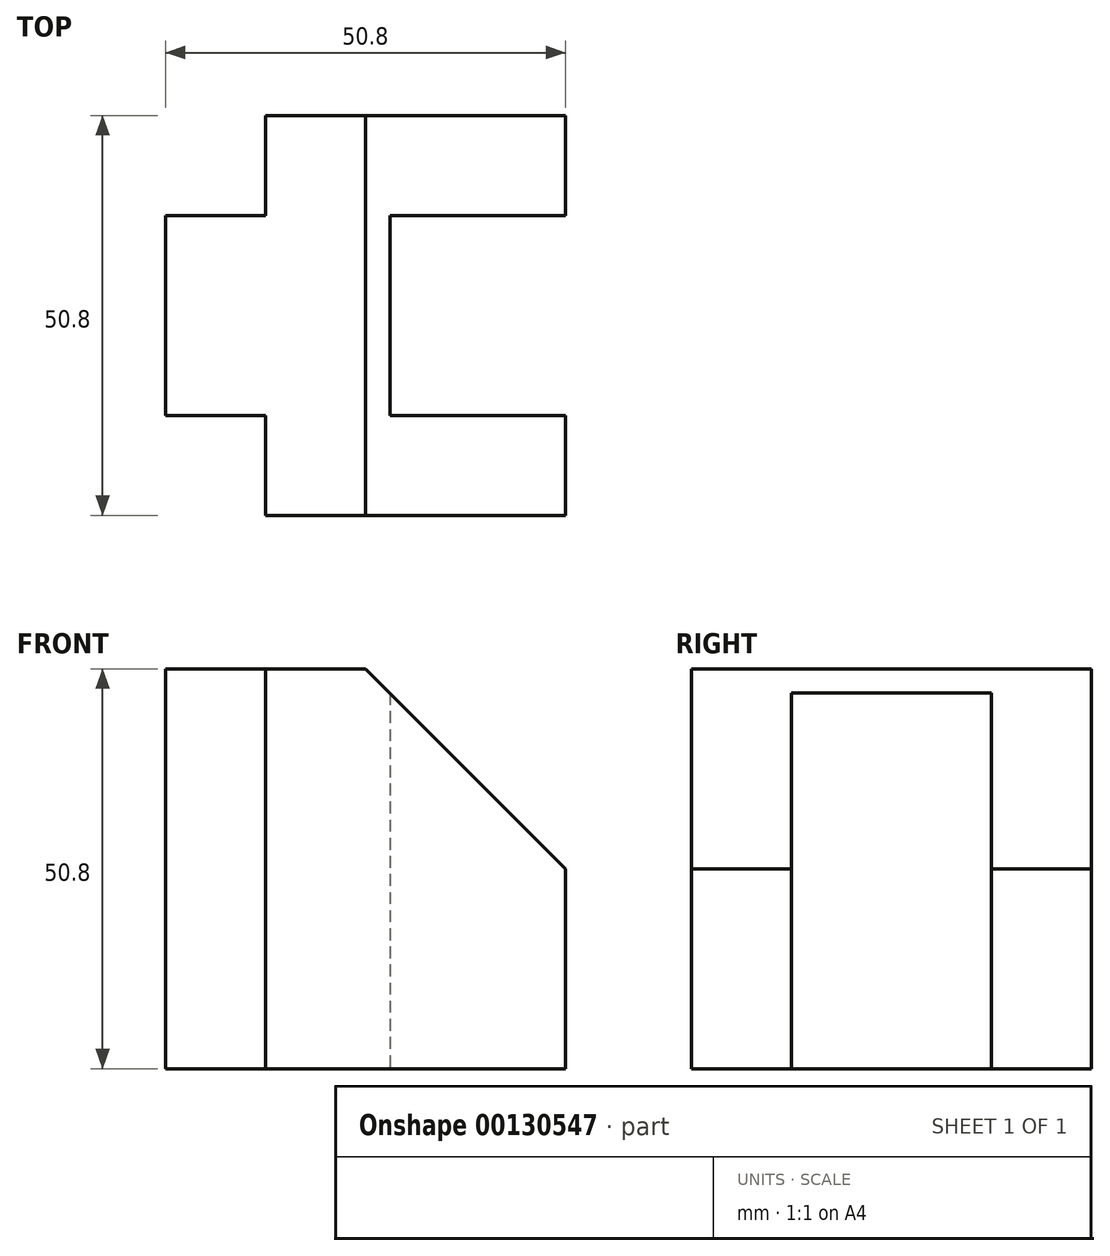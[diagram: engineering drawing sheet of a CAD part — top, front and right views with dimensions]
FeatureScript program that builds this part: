
annotation { "Feature Type Name" : "Feature", "Feature Type Description" : "" }
export const myFeature = defineFeature(function(context is Context, id is Id, definition is map)
    precondition{}
    {
        {
            var Q0;
            Q0=qCreatedBy(makeId("Front.planeOp"),FACE);
            var sketch = newSketch(context, id + "F0", { "sketchPlane" : qUnion([Q0])});
            skLineSegment(sketch, "E0.bottom", {"start": v(0, 0) * mm, "end": v(12.7, 0) * mm});
            skLineSegment(sketch, "E0.top", {"start": v(0, 50.8) * mm, "end": v(12.7, 50.8) * mm});
            skLineSegment(sketch, "E0.left", {"start": v(0, 0) * mm, "end": v(0, 50.8) * mm});
            skLineSegment(sketch, "E0.right", {"start": v(12.7, 0) * mm, "end": v(12.7, 50.8) * mm});
            skLineSegment(sketch, "E1", {"start": v(12.7, 0) * mm, "end": v(50.8, 0) * mm});
            skLineSegment(sketch, "E2", {"start": v(50.8, 0) * mm, "end": v(50.8, 25.4) * mm});
            skLineSegment(sketch, "E3", {"start": v(50.8, 25.4) * mm, "end": v(25.4, 50.8) * mm});
            skLineSegment(sketch, "E4", {"start": v(25.4, 50.8) * mm, "end": v(12.7, 50.8) * mm});
            skLineSegment(sketch, "E5", {"start": v(25.4, 50.8) * mm, "end": v(50.8, 50.8) * mm});
            skLineSegment(sketch, "E6", {"start": v(50.8, 50.8) * mm, "end": v(50.8, 25.4) * mm});
            skSolve(sketch);
        }
        {
            var Q0;
            Q0=qCreatedBy(makeId("Top.planeOp"),FACE);
            var sketch = newSketch(context, id + "F1", { "sketchPlane" : qUnion([Q0])});
            skLineSegment(sketch, "E7", {"start": v(0, 38.1) * mm, "end": v(0, 12.7) * mm});
            skLineSegment(sketch, "E8", {"start": v(0, 12.7) * mm, "end": v(12.7, 12.7) * mm});
            skLineSegment(sketch, "E9", {"start": v(12.7, 12.7) * mm, "end": v(12.7, 0) * mm});
            skLineSegment(sketch, "E10", {"start": v(12.7, 0) * mm, "end": v(50.8, 0) * mm});
            skLineSegment(sketch, "E11", {"start": v(50.8, 0) * mm, "end": v(50.8, 12.7) * mm});
            skLineSegment(sketch, "E12", {"start": v(50.8, 12.7) * mm, "end": v(28.48, 12.7) * mm});
            skLineSegment(sketch, "E13", {"start": v(28.48, 12.7) * mm, "end": v(28.48, 38.1) * mm});
            skLineSegment(sketch, "E14", {"start": v(28.48, 38.1) * mm, "end": v(50.8, 38.1) * mm});
            skLineSegment(sketch, "E15", {"start": v(50.8, 38.1) * mm, "end": v(50.8, 50.8) * mm});
            skLineSegment(sketch, "E16", {"start": v(50.8, 50.8) * mm, "end": v(12.7, 50.8) * mm});
            skLineSegment(sketch, "E17", {"start": v(12.7, 50.8) * mm, "end": v(12.7, 38.1) * mm});
            skLineSegment(sketch, "E18", {"start": v(12.7, 38.1) * mm, "end": v(0, 38.1) * mm});
            skLineSegment(sketch, "E19", {"start": v(25.4, 50.8) * mm, "end": v(25.4, 0) * mm});
            skSolve(sketch);
        }
        {
            var Q0;
            Q0=makeQuery(id+"F1.imprint","IMPRINT",FACE,{"disambiguationData":[TD([[makeQuery(id+"F1.imprint","IMPRINT",EDGE,{"derivedFrom":sQuery(id+"F1.wireOp",EDGE,"E7")}),1.0]])]});
            var Q1;
            {var subQ0=sQuery(id+"F1.wireOp",EDGE,"E11");Q1=makeQuery(id+"F1.imprint","IMPRINT",FACE,{"disambiguationData":[TD([[makeQuery(id+"F1.imprint","IMPRINT",EDGE,{"derivedFrom":subQ0}),1.0]])]});}
            extrude(context, id + "F2", {"entities" : qUnion([Q0, Q1]), "depth" : 50.8 * mm});
        }
        {
            var Q0;
            Q0=makeQuery(id+"F0.imprint","IMPRINT",FACE,{"disambiguationData":[TD([[makeQuery(id+"F0.imprint","IMPRINT",EDGE,{"derivedFrom":sQuery(id+"F0.wireOp",EDGE,"E3")}),-1.0]])]});
            extrude(context, id + "F3", {"entities" : qUnion([Q0]), "operationType" : NewBodyOperationType.REMOVE, "endBound" : BoundingType.THROUGH_ALL, "oppositeDirection" : true, "depth" : 25.4 * mm});
        }
    });
